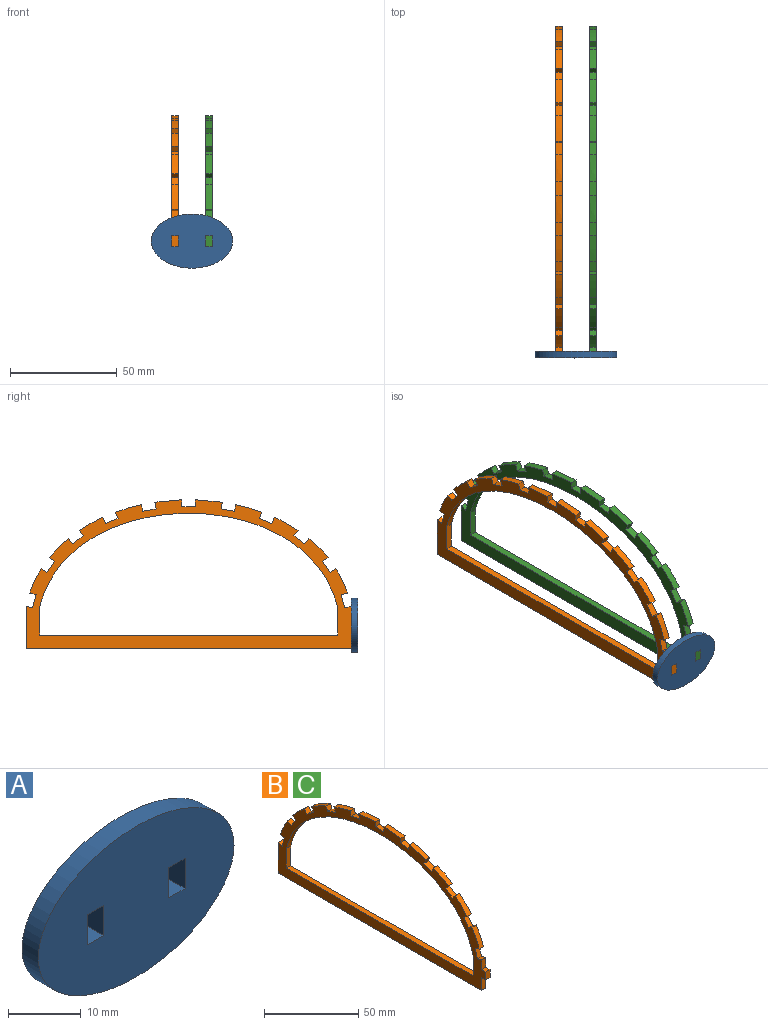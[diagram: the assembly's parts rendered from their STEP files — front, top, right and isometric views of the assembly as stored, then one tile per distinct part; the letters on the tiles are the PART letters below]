
ASSEMBLY  parts=3 mates=2
PART A: 11 faces, bbox 38.1x3.2x25.4 mm
  f0: plane 5.08x3.18mm, normal (1,0,0), area 16.1mm2, adj f1,f8,f9,f10
  f1: plane 3.18x3.18mm, normal (0,0,-1), area 10.1mm2, adj f0,f2,f9,f10
  f2: plane 5.08x3.18mm, normal (-1,0,0), area 16.1mm2, adj f1,f8,f9,f10
  f3: plane 5.08x3.18mm, normal (-1,0,0), area 16.1mm2, adj f4,f7,f9,f10
  f4: plane 3.18x3.18mm, normal (0,0,1), area 10.1mm2, adj f3,f5,f9,f10
  f5: plane 5.08x3.18mm, normal (1,0,0), area 16.1mm2, adj f4,f7,f9,f10
  f6: extruded ~38.1x25.4mm, area 319.9mm2, adj f9,f10
  f7: plane 3.18x3.18mm, normal (0,0,-1), area 10.1mm2, adj f3,f5,f9,f10
  f8: plane 3.18x3.18mm, normal (0,0,1), area 10.1mm2, adj f0,f2,f9,f10
  f9: plane 38.1x25.4mm, normal (0,-1,0), area 727.8mm2, adj f0,f1,f2,f3,f4,f5,f6,f7
  f10: plane 38.1x25.4mm, normal (0,1,0), area 727.8mm2, adj f0,f1,f2,f3,f4,f5,f6,f7
PART B: 56 faces, bbox 3.2x155.6x69.7 mm
  f0: extruded ~139.7x44.24mm, area 566.7mm2, adj f1,f53,f54,f55
  f1: plane 12.83x3.18mm, normal (0,-1,0), area 40.7mm2, adj f0,f2,f54,f55
  f2: plane 139.7x3.18mm, normal (0,0,1), area 443.5mm2, adj f1,f53,f54,f55
  f3: extruded ~9x8.96mm, area 40.4mm2, adj f4,f52,f54,f55
  f4: plane 3.18x2.59mm, normal (0,-0.58,-0.81), area 10.1mm2, adj f3,f5,f54,f55
  f5: plane 5.17x3.69mm, normal (0,-0.81,0.58), area 20.2mm2, adj f4,f6,f54,f55
  f6: plane 3.18x2.59mm, normal (0,0.58,0.81), area 10.1mm2, adj f5,f7,f54,f55
  f7: extruded ~11.46x5.46mm, area 40.4mm2, adj f6,f8,f54,f55
  f8: plane 3.18x3.06mm, normal (0,-0.27,-0.96), area 10.1mm2, adj f7,f9,f54,f55
  f9: plane 6.12x3.18mm, normal (0,-0.96,0.27), area 20.2mm2, adj f8,f10,f54,f55
  f10: plane 3.18x3.06mm, normal (0,0.27,0.96), area 10.1mm2, adj f9,f11,f54,f55
  f11: plane 6.35x3.18mm, normal (0,-1,0), area 20.2mm2, adj f10,f12,f54,f55
  f12: plane 3.18x3.18mm, normal (0,0,1), area 10.1mm2, adj f11,f13,f54,f55
  f13: plane 5.08x3.18mm, normal (0,-1,0), area 16.1mm2, adj f12,f14,f54,f55
  f14: plane 3.18x3.18mm, normal (0,0,-1), area 10.1mm2, adj f13,f15,f54,f55
  f15: plane 8.46x3.18mm, normal (0,-1,0), area 26.9mm2, adj f14,f16,f54,f55
  f16: plane 152.4x3.18mm, normal (0,0,-1), area 483.9mm2, adj f15,f17,f54,f55
  f17: plane 19.89x3.18mm, normal (0,1,0), area 63.1mm2, adj f16,f18,f54,f55
  f18: plane 3.18x3.06mm, normal (0,-0.27,0.96), area 10.1mm2, adj f17,f19,f54,f55
  f19: plane 6.12x3.18mm, normal (0,0.96,0.27), area 20.2mm2, adj f18,f20,f54,f55
  f20: plane 3.18x3.06mm, normal (0,0.27,-0.96), area 10.1mm2, adj f19,f21,f54,f55
  f21: extruded ~11.46x5.46mm, area 40.4mm2, adj f20,f22,f54,f55
  f22: plane 3.18x2.59mm, normal (0,-0.58,0.81), area 10.1mm2, adj f21,f23,f54,f55
  f23: plane 5.17x3.69mm, normal (0,0.81,0.58), area 20.2mm2, adj f22,f24,f54,f55
  f24: plane 3.18x2.59mm, normal (0,0.58,-0.81), area 10.1mm2, adj f23,f25,f54,f55
  f25: extruded ~9x8.96mm, area 40.4mm2, adj f24,f26,f54,f55
  f26: plane 3.18x2.55mm, normal (0,-0.8,0.59), area 10.1mm2, adj f25,f27,f54,f55
  f27: plane 5.11x3.77mm, normal (0,0.59,0.8), area 20.2mm2, adj f26,f28,f54,f55
  f28: plane 3.18x2.55mm, normal (0,0.8,-0.59), area 10.1mm2, adj f27,f29,f54,f55
  f29: extruded ~11.12x6.14mm, area 40.4mm2, adj f28,f30,f54,f55
  f30: plane 3.18x2.94mm, normal (0,-0.93,0.38), area 10.1mm2, adj f29,f31,f54,f55
  f31: plane 5.88x3.18mm, normal (0,0.38,0.93), area 20.2mm2, adj f30,f32,f54,f55
  f32: plane 3.18x2.94mm, normal (0,0.93,-0.38), area 10.1mm2, adj f31,f33,f54,f55
  f33: extruded ~12.21x3.5mm, area 40.4mm2, adj f32,f34,f54,f55
  f34: plane 3.18x3.12mm, normal (0,-0.98,0.18), area 10.1mm2, adj f33,f35,f54,f55
  f35: plane 6.25x3.18mm, normal (0,0.18,0.98), area 20.2mm2, adj f34,f36,f54,f55
  f36: plane 3.18x3.12mm, normal (0,0.98,-0.18), area 10.1mm2, adj f35,f37,f54,f55
  f37: extruded ~12.65x3.18mm, area 40.3mm2, adj f36,f38,f54,f55
  f38: plane 3.18x3.18mm, normal (0,-1,0), area 10.1mm2, adj f37,f39,f54,f55
  f39: plane 6.35x3.18mm, normal (0,0,1), area 20.2mm2, adj f38,f40,f54,f55
  f40: plane 3.18x3.18mm, normal (0,1,0), area 10.1mm2, adj f39,f41,f54,f55
  f41: extruded ~12.65x3.18mm, area 40.3mm2, adj f40,f42,f54,f55
  f42: plane 3.18x3.12mm, normal (0,-0.98,-0.18), area 10.1mm2, adj f41,f43,f54,f55
  f43: plane 6.25x3.18mm, normal (0,-0.18,0.98), area 20.2mm2, adj f42,f44,f54,f55
  f44: plane 3.18x3.12mm, normal (0,0.98,0.18), area 10.1mm2, adj f43,f45,f54,f55
  f45: extruded ~12.21x3.5mm, area 40.4mm2, adj f44,f46,f54,f55
  f46: plane 3.18x2.94mm, normal (0,-0.93,-0.38), area 10.1mm2, adj f45,f47,f54,f55
  f47: plane 5.88x3.18mm, normal (0,-0.38,0.93), area 20.2mm2, adj f46,f48,f54,f55
  f48: plane 3.18x2.94mm, normal (0,0.93,0.38), area 10.1mm2, adj f47,f49,f54,f55
  f49: extruded ~11.12x6.14mm, area 40.4mm2, adj f48,f50,f54,f55
  f50: plane 3.18x2.55mm, normal (0,-0.8,-0.59), area 10.1mm2, adj f49,f51,f54,f55
  f51: plane 5.11x3.77mm, normal (0,-0.59,0.8), area 20.2mm2, adj f50,f52,f54,f55
  f52: plane 3.18x2.55mm, normal (0,0.8,0.59), area 10.1mm2, adj f3,f51,f54,f55
  f53: plane 12.83x3.18mm, normal (0,1,0), area 40.7mm2, adj f0,f2,f54,f55
  f54: plane 155.58x69.72mm, normal (1,0,0), area 2118.6mm2, adj f0,f1,f2,f3,f4,f5,f6,f7
  f55: plane 155.58x69.72mm, normal (-1,0,0), area 2118.6mm2, adj f0,f1,f2,f3,f4,f5,f6,f7
PART C: same geometry as B
PLACE A t=(-10.94,-4.26,0.7)mm
PLACE B t=(-20.47,-7.44,-1.84)mm
PLACE C t=(-4.59,-7.44,-1.84)mm
MATE fastened B.f14 <-> A.f4  axis (0,0,-1) through (-20.47,-7.44,-1.84)mm
MATE fastened C.f14 <-> A.f8  axis (0,0,-1) through (-4.59,-7.44,-1.84)mm
